# Revit family: PRD_AR_FlshCntrlDvcs_F5EElectronicUrinalFlushValve_F5EF3010
name_source: partatom
category: Specialty Equipment
units: mm (PartAtom-declared; Revit-internal decimal feet)

## family parameters
Cut with Voids When Loaded = No
Enable Cutting in Views = No
Host = Face
Maintain Annotation Orientation = No
OmniClass Number = 23.40.20.21
OmniClass Title = Toilet and Bath Specialties
Part Type = Normal
Room Calculation Point = No
Round Connector Dimension = Use Diameter
Shared = No

## types (1)
- F5EF3010
    AssetType = Fixed
    BIMObjectName = PRD_AR_FlushControlDevices_F5EElectronicUrinalFlushValve_F5EF3010
    BodyMaterial = PRD_AR_StainlessSteel_SatinFinished
    BuiltInFittingModel = Finishing section
    Category = Pr_75_50_46_31, Flush control devices
    CoverPlateHeight = 150
    CoverPlateWidth = 120
    Default Elevation = 900 mm  [stored 2.95276 ft]
    DefaultAutomaticHygieneFlush = 24h after the last activity
    Description = F5E urinal flush valve DN 15 and installation kit for in-wall installation with basic installation kit, opto-electronically controlled. With self-closing solenoid valve cartridge, holding frame, stainless steel cover plate 120 x 150 mm with covered screw fixing including sensor with control electronics and strainer. Activated water hygiene flushing 24 hours after last activation and saving of statistical data. With option for parametrisation and communication via optional, bidirectional remote control. Option for battery operation with 6 V lithium battery (CR-P2) per fitting or separate power supply via power supply unit 6.75 V/12 V DC or AQUA 3000 open system accessories. Battery compartment including battery or power supply unit with extension cable must be ordered separately.
    DiameterNominal = DN15
    DurationUnit = year
    Export Type to IFC As = IfcSensorType
    Features = Opto-electronically controlled. Stainless steel cover plate 120 x 150 mm with covered screw fixing including sensor with control electronics and strainer. Battery compartment including battery or power supply unit with extension cable must be ordered separately.
    Finish = satin finished
    FunctionalPrinciple = electronic self-closing
    HygieneFlushing = Yes
    IfcExportAs = IfcSensorType
    IfcExportType = USERDEFINED
    Manufacturer = KWC Group Management AG
    ManufacturerName = KWC Group Management AG
    ManufacturerURL = www.kwc-professional.com
    Material = stainless steel
    MaterialCasing = stainless steel
    MaterialFitting = brass-look
    MinimumFlowPressure = 1 bar
    Model = F5EF3010
    ModelNumber = 2030067743
    ModelReference = F5EF3010
    NBSDescription = Flush control devices
    NBSReference = 90-15-35/470
    Name = F5E Electronic urinal flush valve F5EF3010
    NominalDepth = 10 mm  [stored 0.0328084 ft]
    NominalHeight = 150 mm
    NominalWidth = 120 mm  [stored 0.393701 ft]
    Parameterization = remote control
    PowerSupplyConnection = 6,75 / 12 V DC / A3000 open
    ProductInformation = http://pim.kwc.com
    Status = New
    SurfaceFinishCasing = satin finished
    Type IFC Predefined Type = USERDEFINED
    TypeOfFlushingFitting = urinal flush valve
    TypeOfMounting = in-wall installation with box
    TypeOfOperation = sensor operation
    TypeOfPowerSupply = Other
    TypeOfSensor = opto-electronic sensor
    URL = www.kwc-professional.com
    Uniclass2015Code = Pr_75_50_46_31
    Uniclass2015Title = Flush control devices
    Uniclass2015Version = Products v1.32
    Version = 1
    WarrantyDurationUnit = year
    WithTransformerPowerSupply = No

note: [stored X ft] marks values corroborated as IEEE doubles in the binary element streams (Revit-internal decimal feet)

## geometry (parser evidence)
native form markers: Sweep x5
no freeform markers — native parametric forms only
